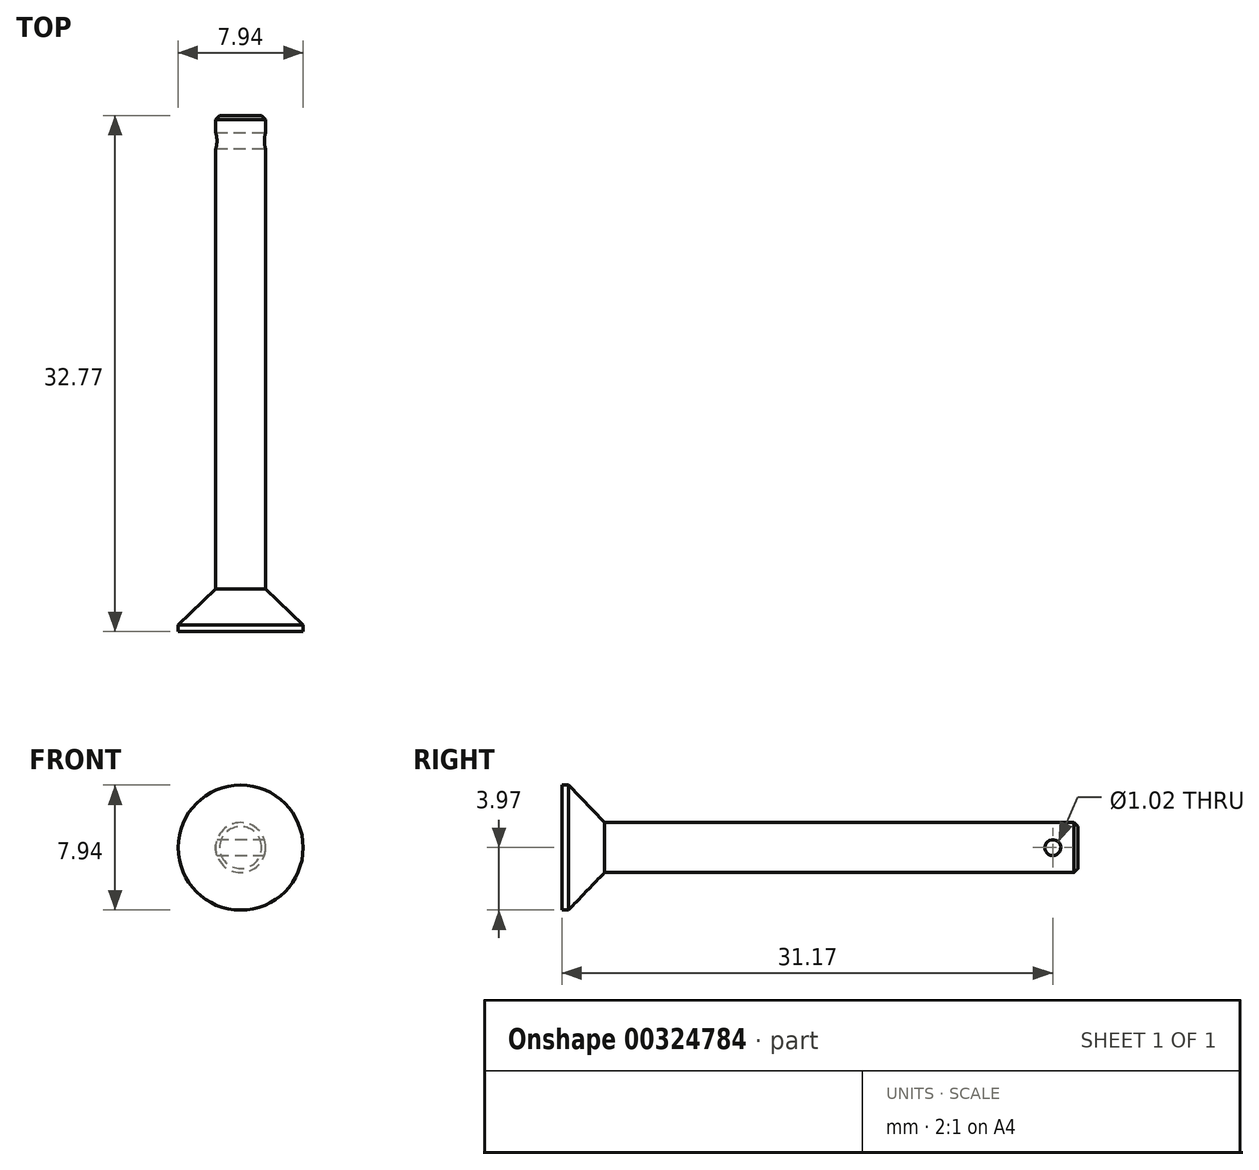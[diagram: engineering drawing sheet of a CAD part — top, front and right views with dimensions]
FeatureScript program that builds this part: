
annotation { "Feature Type Name" : "Feature", "Feature Type Description" : "" }
export const myFeature = defineFeature(function(context is Context, id is Id, definition is map)
    precondition{}
    {
        {
            var Q0;
            Q0=qCreatedBy(makeId("Front.planeOp"),FACE);
            var sketch = newSketch(context, id + "F0", { "sketchPlane" : qUnion([Q0])});
            skCircle(sketch, "E0", {"center": v(0, 0) * mm, "radius": 1.59 * mm});
            skSolve(sketch);
        }
        {
            var Q0;
            Q0=makeQuery(id+"F0.imprint","IMPRINT",FACE,{"disambiguationData":[TD([[makeQuery(id+"F0.imprint","IMPRINT",EDGE,{"derivedFrom":sQuery(id+"F0.wireOp",EDGE,"E0")}),1.0]])]});
            extrude(context, id + "F1", {"entities" : qUnion([Q0]), "depth" : 30.07 * mm, "offsetDistance" : 25.4 * mm});
        }
        {
            var Q0;
            Q0=makeQuery(id+"F1.opExtrude","CAP_EDGE",EDGE,{"disambiguationData":[OSD([sQuery(id+"F0.wireOp",EDGE,"E0")])],"isStart":true});
            chamfer(context, id + "F2", {"entities" : qUnion([Q0]), "width" : 0.25 * mm, "tangentPropagation" : true});
        }
        {
            var Q0;
            Q0=qCreatedBy(makeId("Right.planeOp"),FACE);
            var sketch = newSketch(context, id + "F3", { "sketchPlane" : qUnion([Q0])});
            skLineSegment(sketch, "E1", {"start": v(-32.77, 10.63) * mm, "end": v(-32.77, -9.92) * mm, "construction": true});
            skLineSegment(sketch, "E2", {"start": v(-37.15, 3.97) * mm, "end": v(-18.22, 3.97) * mm, "construction": true});
            skLineSegment(sketch, "E3", {"start": v(-30.07, 1.59) * mm, "end": v(-41.59, 1.59) * mm, "construction": true});
            skLineSegment(sketch, "E4", {"start": v(-30.07, 1.59) * mm, "end": v(-32.36, 3.97) * mm});
            skLineSegment(sketch, "E5", {"start": v(-32.36, 3.97) * mm, "end": v(-32.77, 3.97) * mm});
            skLineSegment(sketch, "E6", {"start": v(-32.77, 3.97) * mm, "end": v(-32.77, 0) * mm});
            skLineSegment(sketch, "E7", {"start": v(-32.77, 0) * mm, "end": v(-30.07, 0) * mm});
            skLineSegment(sketch, "E8", {"start": v(-30.07, 0) * mm, "end": v(-30.07, 1.59) * mm});
            skSolve(sketch);
        }
        {
            var Q0;
            Q0=makeQuery(id+"F3.imprint","IMPRINT",FACE,{"disambiguationData":[TD([[makeQuery(id+"F3.imprint","IMPRINT",EDGE,{"derivedFrom":sQuery(id+"F3.wireOp",EDGE,"E4")}),1.0]])]});
            var Q1;
            Q1=makeQuery(id+"F1.opExtrude","CAP_EDGE",EDGE,{"disambiguationData":[OSD([sQuery(id+"F0.wireOp",EDGE,"E0")])],"isStart":false});
            sweep(context, id + "F4", {"operationType" : NewBodyOperationType.ADD, "profiles" : qUnion([Q0]), "path" : qUnion([Q1])});
        }
        {
            var Q0;
            Q0=qCreatedBy(makeId("Right.planeOp"),FACE);
            cPlane(context, id + "F5", {"entities" : qUnion([Q0]), "cplaneType" : CPlaneType.OFFSET, "offset" : 1.63 * mm, "width" : 152.4 * mm, "height" : 152.4 * mm});
        }
        {
            var Q0;
            Q0=qCreatedBy(id+"F5.planeOp",FACE);
            var sketch = newSketch(context, id + "F6", { "sketchPlane" : qUnion([Q0])});
            skCircle(sketch, "E9", {"center": v(-1.6, 0) * mm, "radius": 0.5 * mm});
            skSolve(sketch);
        }
        {
            var Q0;
            Q0=makeQuery(id+"F6.imprint","IMPRINT",FACE,{"disambiguationData":[TD([[makeQuery(id+"F6.imprint","IMPRINT",EDGE,{"derivedFrom":sQuery(id+"F6.wireOp",EDGE,"E9")}),1.0]])]});
            extrude(context, id + "F7", {"entities" : qUnion([Q0]), "operationType" : NewBodyOperationType.REMOVE, "endBound" : BoundingType.THROUGH_ALL, "oppositeDirection" : true, "depth" : 25.4 * mm, "offsetDistance" : 25.4 * mm});
        }
    });
